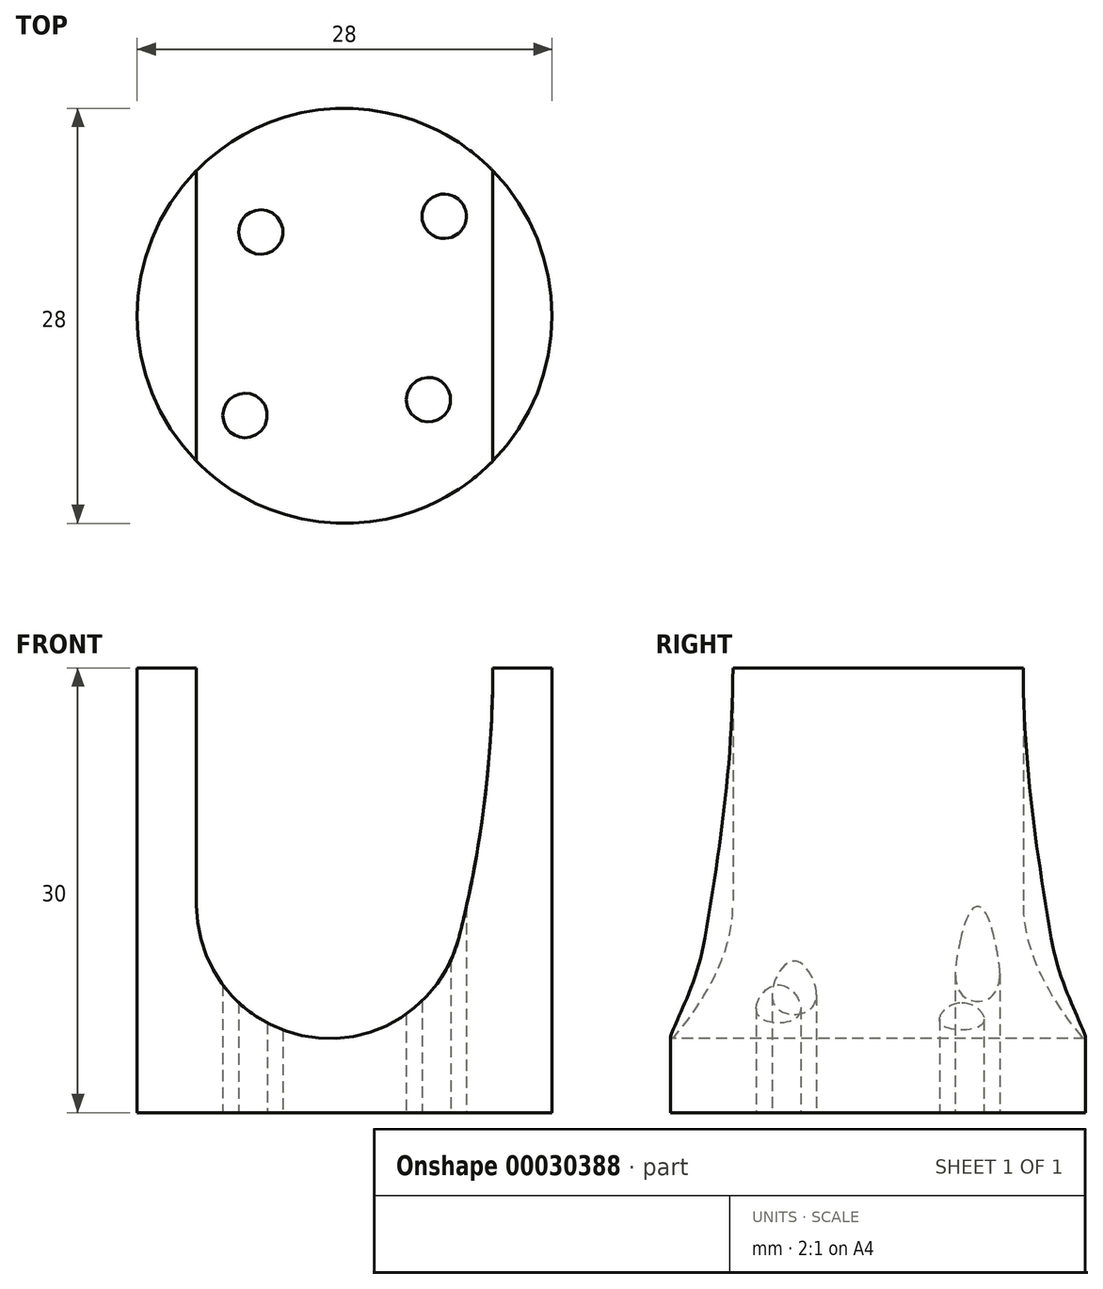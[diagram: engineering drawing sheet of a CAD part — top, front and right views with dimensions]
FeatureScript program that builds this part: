
annotation { "Feature Type Name" : "Feature", "Feature Type Description" : "" }
export const myFeature = defineFeature(function(context is Context, id is Id, definition is map)
    precondition{}
    {
        {
            var Q0;
            Q0=qCreatedBy(makeId("Top.planeOp"),FACE);
            var sketch = newSketch(context, id + "F0", { "sketchPlane" : qUnion([Q0])});
            skCircle(sketch, "E0", {"center": v(0, 0) * mm, "radius": 14 * mm});
            skLineSegment(sketch, "E1", {"start": v(5.66, -5.66) * mm, "end": v(-5.66, 5.66) * mm, "construction": true});
            skLineSegment(sketch, "E2", {"start": v(6.72, 6.72) * mm, "end": v(-6.72, -6.72) * mm, "construction": true});
            skPoint(sketch, "E3", {"position": v(6.72, 6.72) * mm});
            skCircle(sketch, "E4", {"center": v(6.72, 6.72) * mm, "radius": 1.5 * mm});
            skCircle(sketch, "E5", {"center": v(-5.66, 5.66) * mm, "radius": 1.5 * mm});
            skCircle(sketch, "E6", {"center": v(-6.72, -6.72) * mm, "radius": 1.5 * mm});
            skCircle(sketch, "E7", {"center": v(5.66, -5.66) * mm, "radius": 1.5 * mm});
            skSolve(sketch);
        }
        {
            var Q0;
            Q0=makeQuery(id+"F0.imprint","IMPRINT",FACE,{"disambiguationData":[TD([[makeQuery(id+"F0.imprint","IMPRINT",EDGE,{"derivedFrom":sQuery(id+"F0.wireOp",EDGE,"E0")}),1.0]])]});
            var Q1;
            Q1=sQuery(id+"F0.wireOp",EDGE,"E0");
            extrude(context, id + "F1", {"entities" : qUnion([Q0]), "surfaceEntities" : qUnion([Q1]), "depth" : 30 * mm});
        }
        {
            var Q0;
            Q0=qCreatedBy(makeId("Front.planeOp"),FACE);
            var sketch = newSketch(context, id + "F2", { "sketchPlane" : qUnion([Q0])});
            skLineSegment(sketch, "E8", {"start": v(-10, 30) * mm, "end": v(-10, 0) * mm});
            skLineSegment(sketch, "E9.0", {"start": v(-14, 30) * mm, "end": v(14, 30) * mm, "construction": true});
            skLineSegment(sketch, "E10", {"start": v(14, 104.5) * mm, "end": v(14, 0) * mm, "construction": true});
            skLineSegment(sketch, "E11", {"start": v(-14, 0) * mm, "end": v(-14, 30) * mm, "construction": true});
            skLineSegment(sketch, "E12", {"start": v(10, 30) * mm, "end": v(10, 0) * mm});
            skArc(sketch, "E13", {"start": v(-10, 13.99) * mm, "mid": v(-2.14, 5.07) * mm, "end": v(7.7, 11.76) * mm});
            skArc(sketch, "E14", {"start": v(7.7, 11.76) * mm, "mid": v(9.42, 20.8) * mm, "end": v(10, 30) * mm});
            skLineSegment(sketch, "E15", {"start": v(-10, 30) * mm, "end": v(10, 30) * mm});
            skSolve(sketch);
        }
        {
            var Q0;
            Q0 = qSketchRegion(id + "F2", true);
            extrude(context, id + "F3", {"entities" : qUnion([Q0]), "operationType" : NewBodyOperationType.REMOVE, "oppositeDirection" : true, "depth" : 25 * mm, "hasSecondDirection" : true, "secondDirectionOppositeDirection" : false, "secondDirectionDepth" : 25 * mm});
        }
    });
